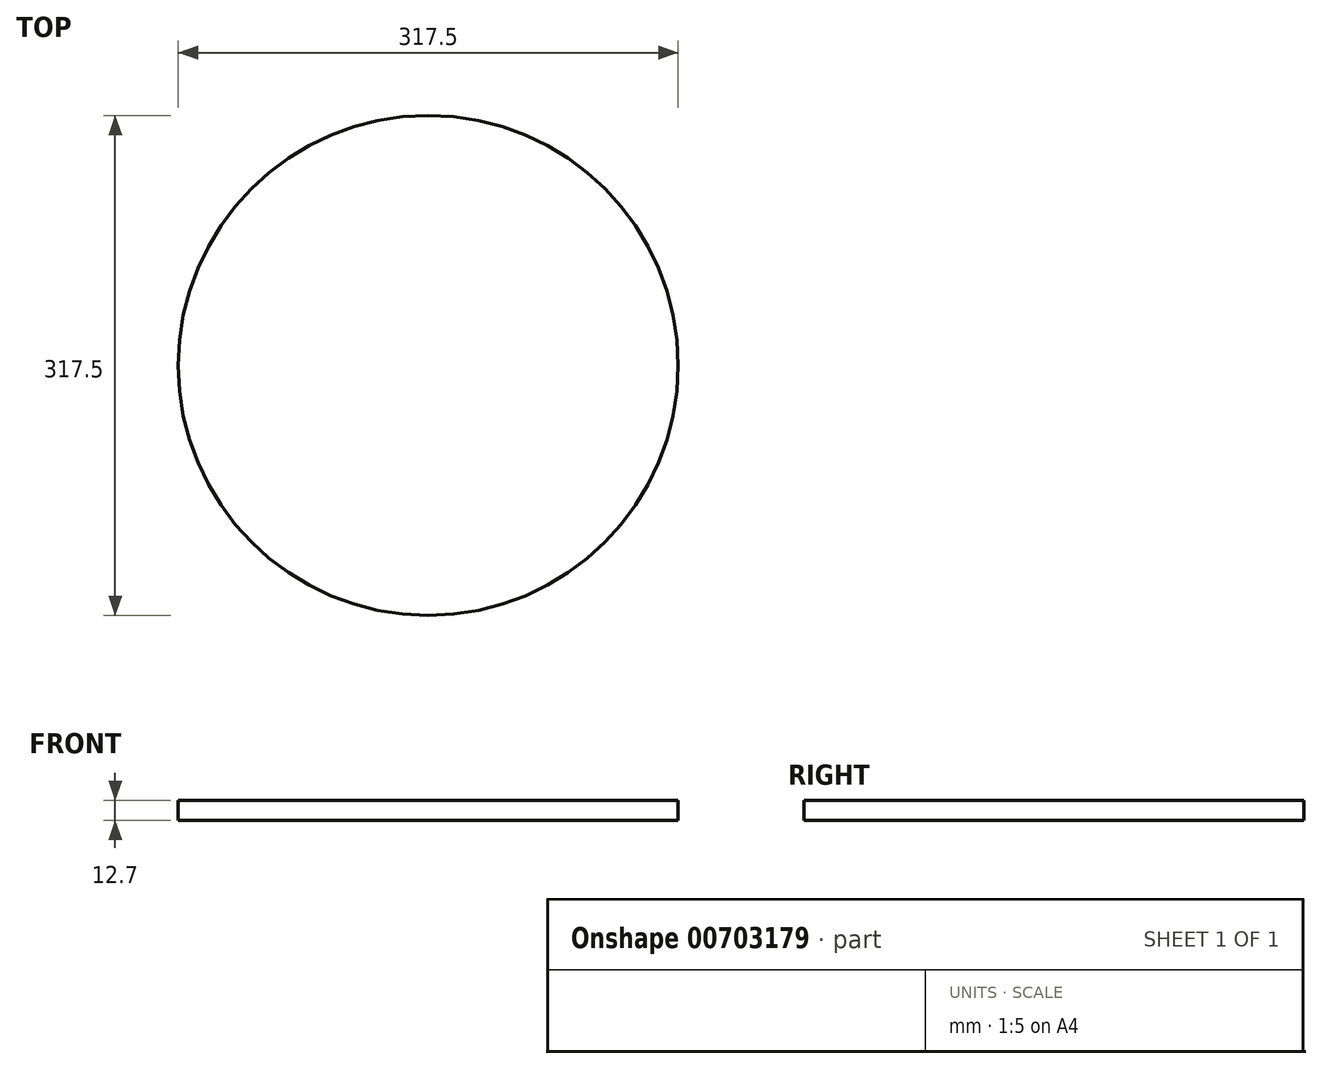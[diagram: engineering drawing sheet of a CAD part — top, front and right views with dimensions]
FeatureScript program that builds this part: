
annotation { "Feature Type Name" : "Feature", "Feature Type Description" : "" }
export const myFeature = defineFeature(function(context is Context, id is Id, definition is map)
    precondition{}
    {
        {
            var Q0;
            Q0=qCreatedBy(makeId("Top.planeOp"),FACE);
            var sketch = newSketch(context, id + "F0", { "sketchPlane" : qUnion([Q0])});
            skCircle(sketch, "E0", {"center": v(0, 0) * mm, "radius": 158.75 * mm});
            skSolve(sketch);
        }
        {
            var Q0;
            Q0 = qSketchRegion(id + "F0", true);
            extrude(context, id + "F1", {"entities" : qUnion([Q0]), "depth" : 12.7 * mm, "offsetDistance" : 25.4 * mm});
        }
    });
